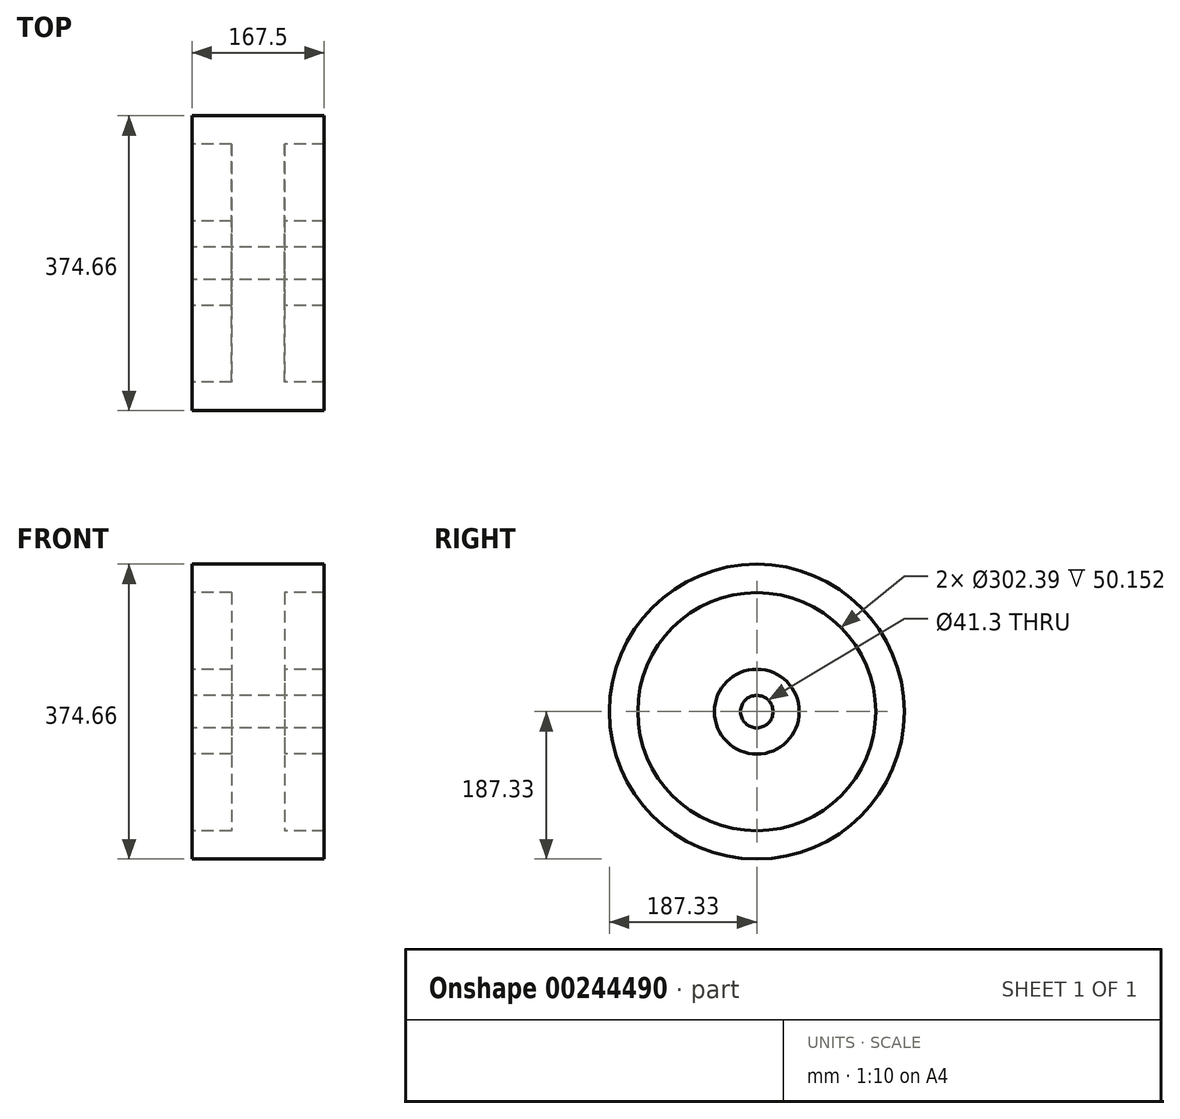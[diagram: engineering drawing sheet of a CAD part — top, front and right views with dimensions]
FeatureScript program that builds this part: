
annotation { "Feature Type Name" : "Feature", "Feature Type Description" : "" }
export const myFeature = defineFeature(function(context is Context, id is Id, definition is map)
    precondition{}
    {
        {
            var Q0;
            Q0=qCreatedBy(makeId("Front.planeOp"),FACE);
            var sketch = newSketch(context, id + "F0", { "sketchPlane" : qUnion([Q0])});
            skLineSegment(sketch, "E0", {"start": v(-98.74, 0) * mm, "end": v(109.1, 0) * mm, "construction": true});
            skSolve(sketch);
        }
        {
            var Q0;
            Q0=qCreatedBy(makeId("Front.planeOp"),FACE);
            var sketch = newSketch(context, id + "F1", { "sketchPlane" : qUnion([Q0])});
            skLineSegment(sketch, "E1", {"start": v(83.75, 187.33) * mm, "end": v(-83.75, 187.33) * mm});
            skLineSegment(sketch, "E2", {"start": v(-83.75, 187.33) * mm, "end": v(-83.75, 151.2) * mm});
            skLineSegment(sketch, "E3", {"start": v(-83.75, 151.2) * mm, "end": v(-33.6, 151.2) * mm});
            skLineSegment(sketch, "E4", {"start": v(-33.6, 151.2) * mm, "end": v(-33.6, 53.84) * mm});
            skLineSegment(sketch, "E5", {"start": v(-33.6, 53.84) * mm, "end": v(-83.75, 53.84) * mm});
            skLineSegment(sketch, "E6", {"start": v(-83.75, 53.84) * mm, "end": v(-83.75, 20.65) * mm});
            skLineSegment(sketch, "E7", {"start": v(83.75, 187.33) * mm, "end": v(83.75, 151.2) * mm});
            skLineSegment(sketch, "E8", {"start": v(83.75, 151.2) * mm, "end": v(33.6, 151.2) * mm});
            skLineSegment(sketch, "E9", {"start": v(33.6, 151.2) * mm, "end": v(33.6, 53.84) * mm});
            skLineSegment(sketch, "E10", {"start": v(33.6, 53.84) * mm, "end": v(83.75, 53.84) * mm});
            skLineSegment(sketch, "E11", {"start": v(83.75, 53.84) * mm, "end": v(83.75, 20.65) * mm});
            skLineSegment(sketch, "E12", {"start": v(83.75, 20.65) * mm, "end": v(-83.75, 20.65) * mm});
            skLineSegment(sketch, "E13", {"start": v(0, 0) * mm, "end": v(0, 225.68) * mm, "construction": true});
            skSolve(sketch);
        }
        {
            var Q0;
            Q0 = qSketchRegion(id + "F1", true);
            var Q1;
            Q1=sQuery(id+"F0.wireOp",EDGE,"E0");
            revolve(context, id + "F2", {"entities" : qUnion([Q0]), "axis" : qUnion([Q1]), "revolveType" : RevolveType.FULL});
        }
    });
